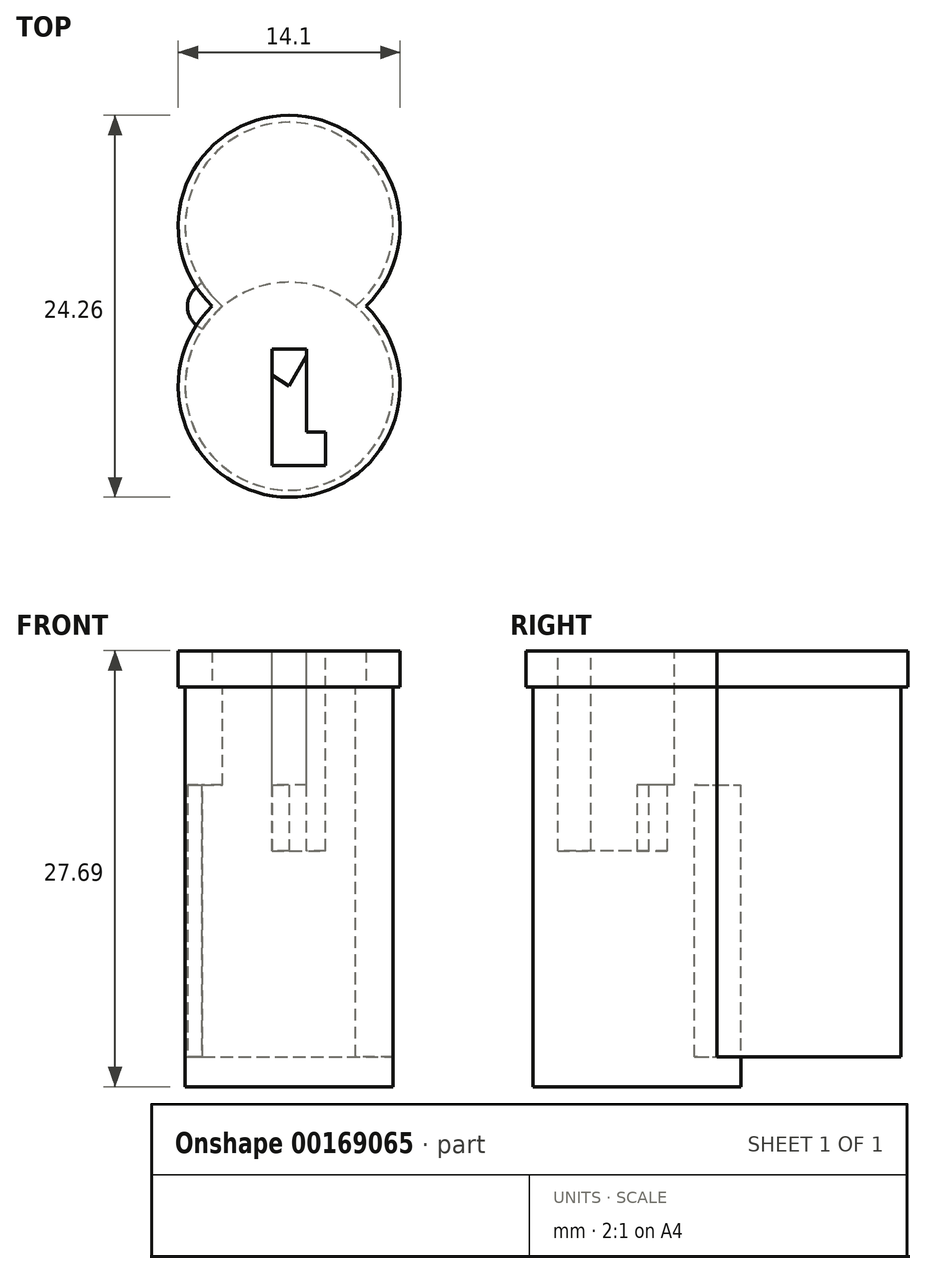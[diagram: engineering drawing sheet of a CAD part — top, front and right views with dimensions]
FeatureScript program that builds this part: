
annotation { "Feature Type Name" : "Feature", "Feature Type Description" : "" }
export const myFeature = defineFeature(function(context is Context, id is Id, definition is map)
    precondition{}
    {
        {
            var Q0;
            Q0=qCreatedBy(makeId("Top.planeOp"),FACE);
            var sketch = newSketch(context, id + "F0", { "sketchPlane" : qUnion([Q0])});
            skCircle(sketch, "E0", {"center": v(0, 5.08) * mm, "radius": 7.05 * mm});
            skCircle(sketch, "E1", {"center": v(0, -5.08) * mm, "radius": 7.05 * mm});
            skLineSegment(sketch, "E2", {"start": v(0, 5.08) * mm, "end": v(0, -5.08) * mm, "construction": true});
            skSolve(sketch);
        }
        {
            var Q0;
            Q0 = qSketchRegion(id + "F0", true);
            extrude(context, id + "F1", {"entities" : qUnion([Q0]), "depth" : 2.3 * mm});
        }
        {
            var Q0;
            Q0=makeQuery(id+"F1.opExtrude","CAP_FACE",FACE,{"disambiguationData":[OSD([sQuery(id+"F0.wireOp",EDGE,"E0"),sQuery(id+"F0.wireOp",EDGE,"E1")])],"isStart":true});
            var sketch = newSketch(context, id + "F2", { "sketchPlane" : qUnion([Q0])});
            skCircle(sketch, "E3", {"center": v(0, 5.08) * mm, "radius": 6.6 * mm});
            skCircle(sketch, "E4", {"center": v(0, -5.08) * mm, "radius": 6.6 * mm});
            skSolve(sketch);
        }
        {
            var Q0;
            Q0 = qSketchRegion(id + "F2", true);
            extrude(context, id + "F3", {"entities" : qUnion([Q0]), "operationType" : NewBodyOperationType.ADD, "depth" : 23.5 * mm});
        }
        {
            var Q0;
            Q0=makeQuery(id+"F1.opExtrude","CAP_FACE",FACE,{"disambiguationData":[OSD([sQuery(id+"F0.wireOp",EDGE,"E0"),sQuery(id+"F0.wireOp",EDGE,"E1")])],"isStart":false});
            var sketch = newSketch(context, id + "F4", { "sketchPlane" : qUnion([Q0])});
            skLineSegment(sketch, "E5", {"start": v(-1.07, -2.7) * mm, "end": v(-1.07, -10.11) * mm});
            skLineSegment(sketch, "E6", {"start": v(-1.07, -10.11) * mm, "end": v(2.33, -10.11) * mm});
            skLineSegment(sketch, "E7", {"start": v(2.33, -10.11) * mm, "end": v(2.33, -8) * mm});
            skLineSegment(sketch, "E8", {"start": v(2.33, -8) * mm, "end": v(1.12, -8) * mm});
            skLineSegment(sketch, "E9", {"start": v(1.12, -2.7) * mm, "end": v(-1.07, -2.7) * mm});
            skLineSegment(sketch, "E10", {"start": v(1.12, -2.7) * mm, "end": v(1.12, -8) * mm});
            skSolve(sketch);
        }
        {
            var Q0;
            Q0 = qSketchRegion(id + "F4", true);
            extrude(context, id + "F5", {"entities" : qUnion([Q0]), "operationType" : NewBodyOperationType.REMOVE, "oppositeDirection" : true, "depth" : 12.7 * mm});
        }
        {
            var Q0;
            Q0=makeQuery(id+"F3.opExtrude","CAP_FACE",FACE,{"disambiguationData":[OSD([sQuery(id+"F2.wireOp",EDGE,"E3"),sQuery(id+"F2.wireOp",EDGE,"E4")])],"isStart":false});
            var sketch = newSketch(context, id + "F6", { "sketchPlane" : qUnion([Q0])});
            skCircle(sketch, "E11", {"center": v(0, 5.08) * mm, "radius": 6.6 * mm});
            skArc(sketch, "E12.0", {"start": v(4.22, 0) * mm, "mid": v(0, 11.68) * mm, "end": v(-4.22, 0) * mm, "construction": true});
            skSolve(sketch);
        }
        {
            var Q0;
            Q0 = qSketchRegion(id + "F6", true);
            extrude(context, id + "F7", {"entities" : qUnion([Q0]), "operationType" : NewBodyOperationType.ADD, "depth" : 1.9 * mm});
        }
        {
            var Q0;
            Q0=makeQuery(id+"F3.opExtrude","CAP_FACE",FACE,{"disambiguationData":[OSD([sQuery(id+"F2.wireOp",EDGE,"E3"),sQuery(id+"F2.wireOp",EDGE,"E4")])],"isStart":false});
            var sketch = newSketch(context, id + "F8", { "sketchPlane" : qUnion([Q0])});
            skArc(sketch, "E13", {"start": v(-6.01, -1.07) * mm, "mid": v(-1.07, -3.46) * mm, "end": v(4.3, -2.37) * mm});
            skLineSegment(sketch, "E14", {"start": v(4.3, -2.37) * mm, "end": v(0, 5.08) * mm});
            skLineSegment(sketch, "E15", {"start": v(-5.8, 1.25) * mm, "end": v(0, 5.08) * mm});
            skPoint(sketch, "E16.visualSharp", {"position": v(-7.18, 0.34) * mm});
            skArc(sketch, "E16.filletArc", {"start": v(-5.8, 1.25) * mm, "mid": v(-6.46, 0.14) * mm, "end": v(-6.01, -1.07) * mm});
            skLineSegment(sketch, "E17", {"start": v(-4.97, 0) * mm, "end": v(0, 0) * mm});
            skLineSegment(sketch, "E18", {"start": v(0, 5.08) * mm, "end": v(0, 0) * mm, "construction": true});
            skLineSegment(sketch, "E19", {"start": v(-6.47, 7.8) * mm, "end": v(-6.47, -6.08) * mm, "construction": true});
            skSolve(sketch);
        }
        {
            var Q0;
            Q0 = qSketchRegion(id + "F8", true);
            extrude(context, id + "F9", {"entities" : qUnion([Q0]), "operationType" : NewBodyOperationType.ADD, "oppositeDirection" : true, "depth" : 17.25 * mm});
        }
    });
